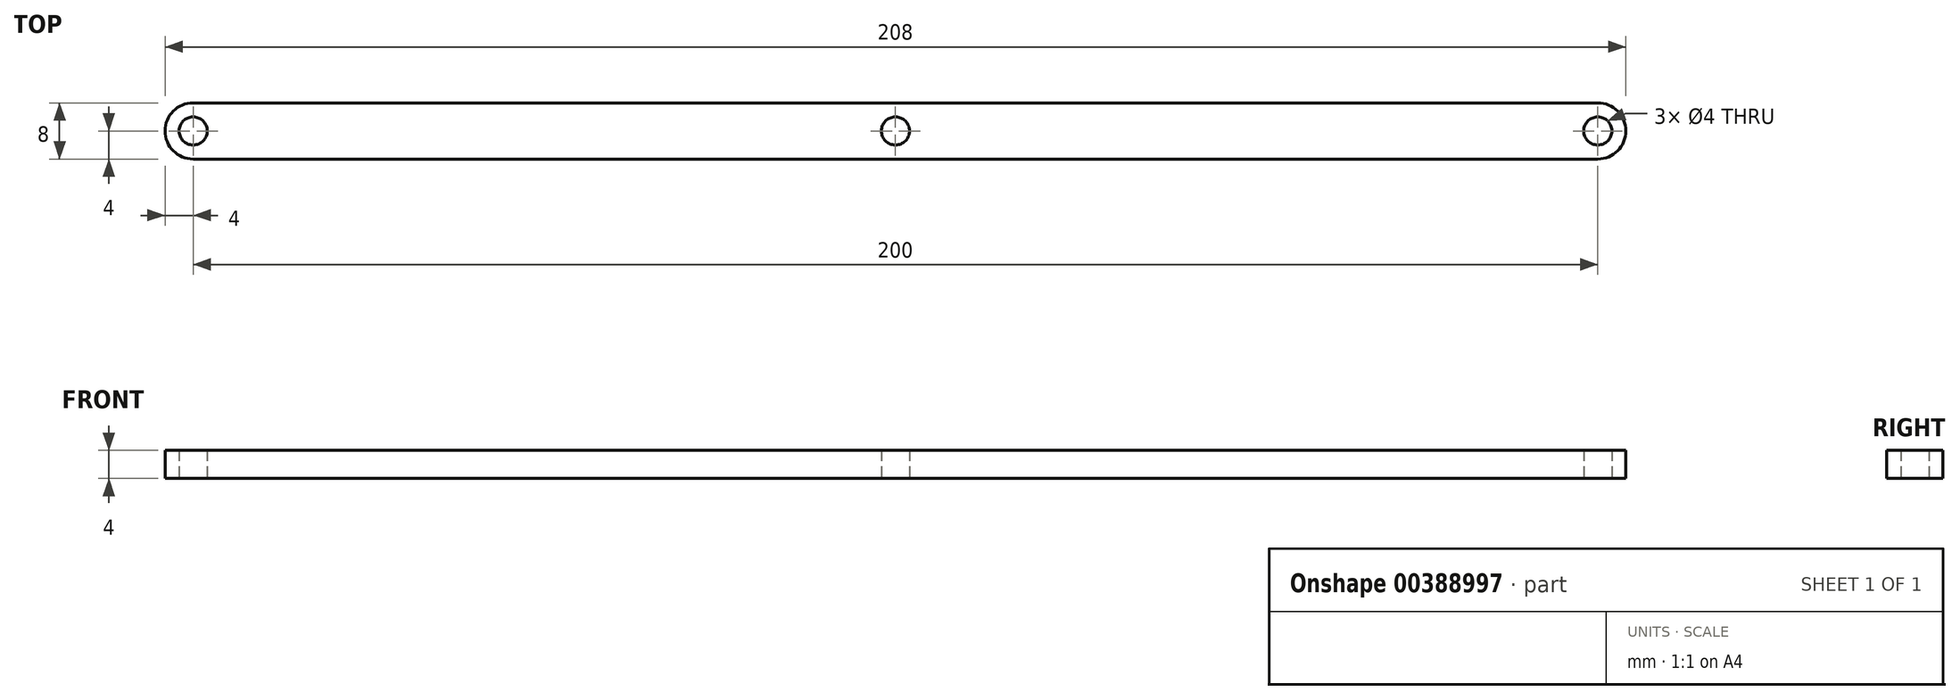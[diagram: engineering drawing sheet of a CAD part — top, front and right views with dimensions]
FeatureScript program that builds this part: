
annotation { "Feature Type Name" : "Feature", "Feature Type Description" : "" }
export const myFeature = defineFeature(function(context is Context, id is Id, definition is map)
    precondition{}
    {
        {
            var Q0;
            Q0=qCreatedBy(makeId("Top.planeOp"), FACE);
            var sketch = newSketch(context, id + "F0", { "sketchPlane" : qUnion([Q0])});
            skCircle(sketch, "E0", {"center": v(0, 0) * mm, "radius": 2 * mm});
            skCircle(sketch, "E1", {"center": v(200, 0) * mm, "radius": 2 * mm});
            skLineSegment(sketch, "E2", {"start": v(0, 0) * mm, "end": v(200, 0) * mm, "construction": true});
            skCircle(sketch, "E3", {"center": v(100, 0) * mm, "radius": 2 * mm});
            skCircle(sketch, "E4", {"center": v(0, 0) * mm, "radius": 4 * mm});
            skCircle(sketch, "E5", {"center": v(200, 0) * mm, "radius": 4 * mm});
            skLineSegment(sketch, "E6", {"start": v(0, 4) * mm, "end": v(200, 4) * mm});
            skLineSegment(sketch, "E7", {"start": v(0, -4) * mm, "end": v(200, -4) * mm});
            skSolve(sketch);
        }
        {
            var Q0;
            Q0 = qSketchRegion(id + "F0", true);
            extrude(context, id + "F1", {"entities" : qUnion([Q0]), "depth" : 4 * mm, "offsetDistance" : 25 * mm});
        }
    });
